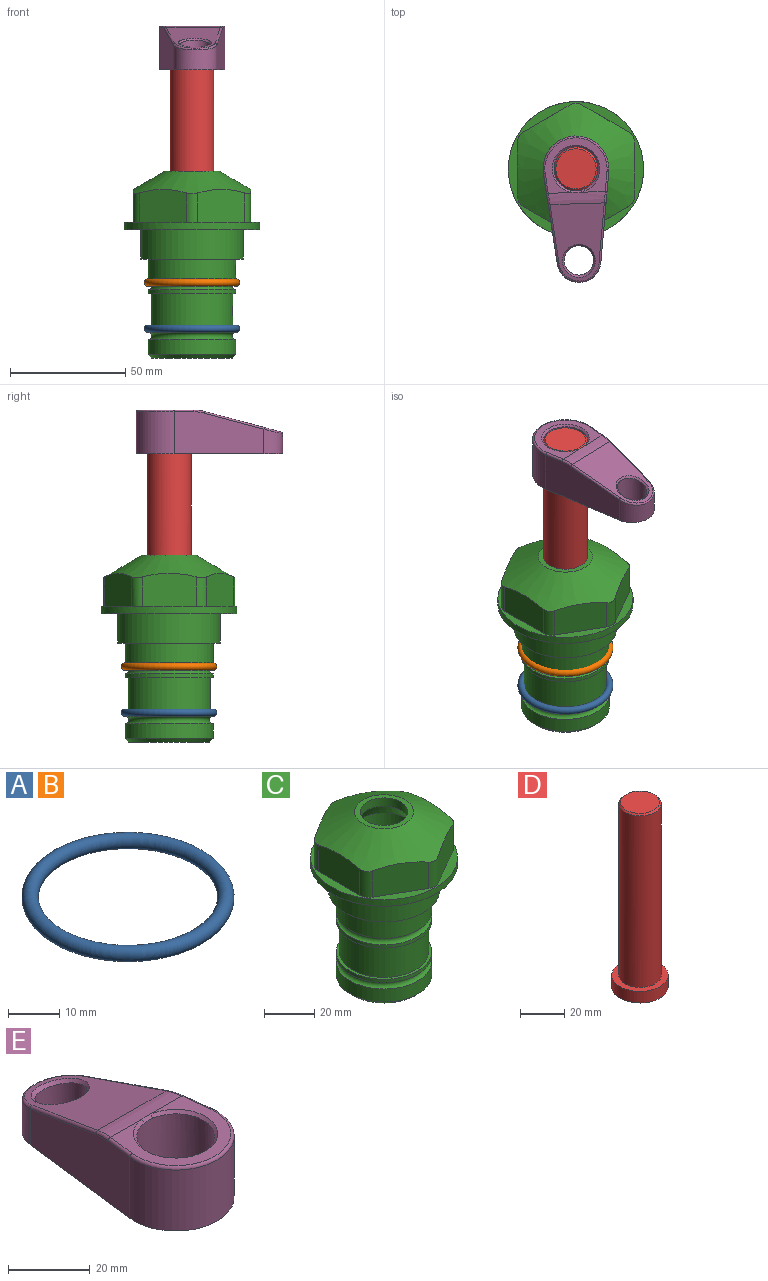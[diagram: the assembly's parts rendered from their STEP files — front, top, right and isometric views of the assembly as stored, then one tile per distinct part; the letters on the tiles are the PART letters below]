
ASSEMBLY  parts=5 mates=4
PART A: 1 faces, bbox 44.7x44.7x3.2 mm
  f0: torus R=19.05mm, axis (0,0,1), area 1193.9mm2
PART B: same geometry as A
PART C: 36 faces, bbox 58.7x58.7x81 mm
  f0: cylinder r=17.78mm len=35.56mm, axis (0,0,1), area 1670.8mm2, adj f23,f24,f31
  f1: cylinder r=19.05mm len=38.1mm, axis (0,0,1), area 1191.9mm2, adj f26,f27,f30
  f2: plane 58.66x58.66mm, normal (0,0,-1), area 1150.6mm2, adj f3,f28
  f3: cylinder r=29.33mm len=58.66mm, axis (0,0,-1), area 585.1mm2, adj f2,f4
  f4: plane 58.66x58.66mm, normal (0,0,1), area 475.9mm2, adj f3,f5,f6,f7,f8,f9,f10,f11
  f5: plane 20.32x14.34mm, normal (-0.5,0.87,0), area 324.4mm2, adj f4,f15,f16,f17
  f6: plane 20.32x14.34mm, normal (0.5,0.87,0), area 324.4mm2, adj f4,f14,f15,f17
  f7: plane 23.48x14.34mm, normal (1,0,0), area 324.4mm2, adj f4,f13,f14,f17
  f8: plane 20.32x14.34mm, normal (0.5,-0.87,0), area 324.4mm2, adj f4,f12,f13,f17
  f9: plane 20.32x14.34mm, normal (-0.5,-0.87,0), area 324.4mm2, adj f4,f11,f12,f17
  f10: plane 23.48x14.34mm, normal (-1,0,0), area 324.4mm2, adj f4,f11,f16,f17
  f11: cylinder r=5.08mm len=12.85mm, axis (0,0,-1), area 67.2mm2, adj f4,f9,f10,f17
  f12: cylinder r=5.08mm len=12.85mm, axis (0,0,-1), area 67.2mm2, adj f4,f8,f9,f17
  f13: cylinder r=5.08mm len=12.85mm, axis (0,0,-1), area 67.2mm2, adj f4,f7,f8,f17
  f14: cylinder r=5.08mm len=12.85mm, axis (0,0,-1), area 67.2mm2, adj f4,f6,f7,f17
  f15: cylinder r=5.08mm len=12.85mm, axis (0,0,-1), area 67.2mm2, adj f4,f5,f6,f17
  f16: cylinder r=5.08mm len=12.85mm, axis (0,0,-1), area 67.2mm2, adj f4,f5,f10,f17
  f17: cone r=11.73mm half-angle=60deg, axis (0,0,-1), area 2071.8mm2, adj f5,f6,f7,f8,f9,f10,f11,f12
  f18: plane 23.46x23.46mm, normal (0,0,1), area 147.4mm2, adj f17,f35
  f19: plane 34.93x34.93mm, normal (0,0,-1), area 958mm2, adj f29
  f20: cylinder r=19.05mm len=38.1mm, axis (0,0,1), area 760.1mm2, adj f21,f29
  f21: torus R=19.05mm, axis (0,0,1), area 565.3mm2, adj f20,f22
  f22: cylinder r=19.05mm len=38.1mm, axis (0,0,1), area 190mm2, adj f21,f23
  f23: plane 38.1x38.1mm, normal (0,0,1), area 146.9mm2, adj f0,f22
  f24: plane 38.1x38.1mm, normal (0,0,-1), area 146.9mm2, adj f0,f25
  f25: cylinder r=19.05mm len=38.1mm, axis (0,0,1), area 190mm2, adj f24,f26
  f26: torus R=19.05mm, axis (0,0,1), area 565.3mm2, adj f1,f25
  f27: plane 44.45x44.45mm, normal (0,0,-1), area 411.7mm2, adj f1,f28
  f28: cylinder r=22.23mm len=44.45mm, axis (0,0,1), area 1773.5mm2, adj f2,f27
  f29: cone r=19.05mm half-angle=45deg, axis (0,0,1), area 257.5mm2, adj f19,f20
  f30: cylinder r=3.17mm len=6.75mm, axis (-1,0,0), area 128mm2, adj f1,f33
  f31: cylinder r=3.17mm len=6.35mm, axis (-1,0,0), area 102.5mm2, adj f0,f33
  f32: plane 25.4x25.4mm, normal (0,0,1), area 506.7mm2, adj f33
  f33: cylinder r=12.7mm len=66.42mm, axis (0,0,-1), area 5236.2mm2, adj f30,f31,f32,f34
  f34: cone r=9.53mm half-angle=30deg, axis (0,0,-1), area 443.4mm2, adj f33,f35
  f35: cylinder r=9.53mm len=19.05mm, axis (0,0,-1), area 240.9mm2, adj f18,f34
PART D: 6 faces, bbox 25.4x25.4x101.6 mm
  f0: plane 17.46x17.46mm, normal (0,0,1), area 239.5mm2, adj f5
  f1: plane 25.4x25.4mm, normal (0,0,-1), area 506.7mm2, adj f2
  f2: cylinder r=12.7mm len=25.4mm, axis (0,0,1), area 506.7mm2, adj f1,f3
  f3: plane 25.4x25.4mm, normal (0,0,1), area 221.7mm2, adj f2,f4
  f4: cylinder r=9.53mm len=94.46mm, axis (0,0,1), area 5653mm2, adj f3,f5
  f5: cone r=8.73mm half-angle=45deg, axis (0,0,-1), area 64.4mm2, adj f0,f4
PART E: 31 faces, bbox 31.7x65.5x19.8 mm
  f0: plane 39.12x18.26mm, normal (0.99,0.12,0), area 612.2mm2, adj f1,f4,f7,f11,f13,f15
  f1: cylinder r=9.53mm len=18.91mm, axis (0,0,-1), area 296.1mm2, adj f0,f2,f7,f17
  f2: plane 39.12x18.26mm, normal (-0.99,0.12,0), area 612.2mm2, adj f1,f4,f7,f12,f14,f16
  f3: cylinder r=6.35mm len=12.7mm, axis (0,0,-1), area 362.4mm2, adj f7,f18
  f4: cylinder r=14.29mm len=28.58mm, axis (0,0,-1), area 882.2mm2, adj f0,f2,f7,f10
  f5: cylinder r=9.53mm len=19.05mm, axis (0,0,-1), area 1092.6mm2, adj f7,f19,f20
  f6: plane 26.99x23.69mm, normal (0,0,1), area 216.2mm2, adj f9,f10,f11,f12,f19
  f7: plane 63.5x28.58mm, normal (0,0,-1), area 661.8mm2, adj f0,f1,f2,f3,f4,f5,f22,f23
  f8: plane 33.52x23.6mm, normal (0,0.26,0.97), area 486mm2, adj f9,f15,f16,f17,f18
  f9: cylinder r=19.05mm len=24.72mm, axis (1,0,0), area 120.4mm2, adj f6,f8,f13,f14,f20
  f10: torus R=13.49mm, axis (0,0,1), area 59mm2, adj f4,f6,f11,f12
  f11: cylinder r=0.79mm len=8.67mm, axis (0.12,-0.99,0), area 10.8mm2, adj f0,f6,f10,f13
  f12: cylinder r=0.79mm len=8.67mm, axis (0.12,0.99,0), area 10.8mm2, adj f2,f6,f10,f14
  f13: bspline ~4.95x1.42mm, area 6.1mm2, adj f0,f9,f11,f15
  f14: bspline ~4.95x1.42mm, area 6.1mm2, adj f2,f9,f12,f16
  f15: cylinder r=0.79mm len=25.95mm, axis (0.12,-0.96,0.26), area 32.9mm2, adj f0,f8,f13,f17
  f16: cylinder r=0.79mm len=25.95mm, axis (0.12,0.96,-0.26), area 32.9mm2, adj f2,f8,f14,f17
  f17: bspline ~18.91x8.38mm, area 30mm2, adj f1,f8,f15,f16
  f18: bspline ~14.29x14.29mm, area 48.3mm2, adj f3,f8
  f19: cone r=9.53mm half-angle=45deg, axis (0,0,1), area 66.5mm2, adj f5,f6,f20
  f20: bspline ~3.22x0.96mm, area 3.5mm2, adj f5,f9,f19
  f21: plane 2.75x2.72mm, normal (0,0,-1), area 2.9mm2, adj f23,f25,f28
  f22: plane 23.05x15.88mm, normal (-0.99,-0.12,0), area 323.6mm2, adj f7,f25,f26,f27,f28,f29
  f23: plane 23.05x15.88mm, normal (0.99,-0.12,0), area 323.6mm2, adj f7,f21,f25,f27,f28,f30
  f24: cylinder r=9.53mm len=10.69mm, axis (0,0,-1), area 114.7mm2, adj f7,f27,f29,f30
  f25: cylinder r=12.7mm len=20.59mm, axis (0,0,-1), area 381.1mm2, adj f7,f21,f22,f23,f26,f28
  f26: plane 2.75x2.72mm, normal (0,0,-1), area 2.9mm2, adj f22,f25,f28
  f27: plane 19.72x18.37mm, normal (0,-0.26,-0.97), area 291.8mm2, adj f22,f23,f24,f28,f29,f30
  f28: cylinder r=15.88mm len=19.92mm, axis (1,0,0), area 54.8mm2, adj f21,f22,f23,f25,f26,f27
  f29: cylinder r=1.59mm len=11mm, axis (0,0,-1), area 34.7mm2, adj f7,f22,f24,f27
  f30: cylinder r=1.59mm len=11mm, axis (0,0,-1), area 34.7mm2, adj f7,f23,f24,f27
PLACE A t=(0,0,-18.41)mm
PLACE B t=(0,0,1.59)mm
PLACE C at identity fixed
PLACE D rot(axis=(0,0,-1),88.1deg) t=(0,0,24.06)mm
PLACE E rot(axis=(0,0,-1),178.1deg) t=(0,0,24.86)mm
MATE fastened D.f2 <-> E.f4  axis (0,0,1) through (0,0,87.56)mm
MATE fastened A.f0 <-> C.f0  axis (0,0,1) through (0,0,-42.93)mm
MATE cylindrical D.f2 <-> C.f0  axis (0,0,-1) through (0,0,-14.04)mm
MATE fastened B.f0 <-> C.f0  axis (0,0,1) through (0,0,-22.92)mm
